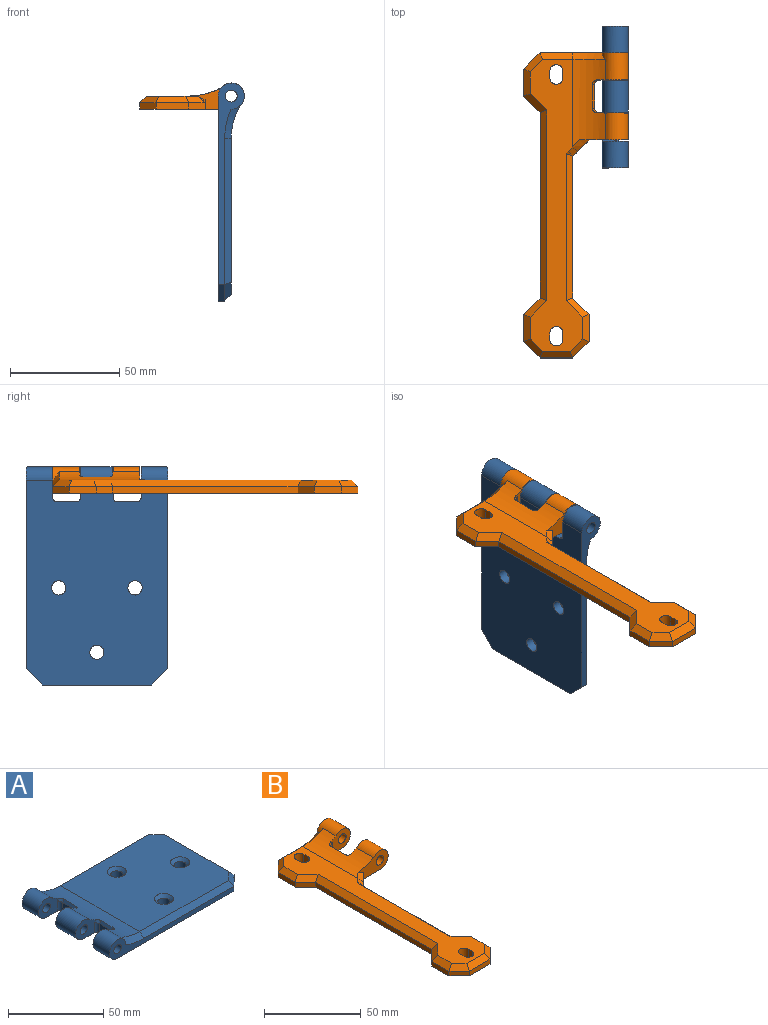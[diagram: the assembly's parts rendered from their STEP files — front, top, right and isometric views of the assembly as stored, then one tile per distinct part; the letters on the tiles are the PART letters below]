
ASSEMBLY  parts=2 mates=1
PART A: 43 faces, bbox 100x65x12 mm
  f0: plane 14.86x12mm, normal (0,-1,0), area 116.3mm2, adj f5,f9,f13,f16,f25,f30
  f1: plane 14.86x12mm, normal (0,1,0), area 116.3mm2, adj f9,f10,f15,f17,f27,f30
  f2: plane 14.86x12mm, normal (0,-1,0), area 116.3mm2, adj f4,f9,f14,f19,f28,f30
  f3: plane 14.86x12mm, normal (0,1,0), area 116.3mm2, adj f5,f9,f13,f18,f24,f30
  f4: cylinder r=6mm len=12.25mm, axis (0,-1,0), area 301.2mm2, adj f2,f6,f9,f30,f36
  f5: cylinder r=6mm len=14.8mm, axis (0,-1,0), area 355.9mm2, adj f0,f3,f9,f30
  f6: plane 92.5x12mm, normal (0,1,0), area 351mm2, adj f4,f9,f14,f35,f36,f37
  f7: plane 92.5x12mm, normal (0,-1,0), area 351mm2, adj f9,f10,f15,f34,f41,f42
  f8: plane 50x3mm, normal (1,0,0), area 150mm2, adj f9,f34,f35,f39
  f9: plane 94x65mm, normal (0,0,-1), area 5700.6mm2, adj f0,f1,f2,f3,f4,f5,f6,f7
  f10: cylinder r=6mm len=12.25mm, axis (0,-1,0), area 301.2mm2, adj f1,f7,f9,f30,f42
  f11: plane 8.85x5.44mm, normal (-1,0,0), area 48.2mm2, adj f9,f16,f17,f26
  f12: plane 8.85x5.44mm, normal (-1,0,0), area 48.2mm2, adj f9,f18,f19,f23
  f13: cylinder r=2.75mm len=14.8mm, axis (0,1,0), area 255.7mm2, adj f0,f3
  f14: cylinder r=2.75mm len=12.25mm, axis (0,1,0), area 211.7mm2, adj f2,f6
  f15: cylinder r=2.75mm len=12.25mm, axis (0,1,0), area 211.7mm2, adj f1,f7
  f16: cylinder r=2mm len=6.72mm, axis (0,0,-1), area 19.1mm2, adj f0,f9,f11,f25
  f17: cylinder r=2mm len=6.72mm, axis (0,0,1), area 19.1mm2, adj f1,f9,f11,f27
  f18: cylinder r=2mm len=6.72mm, axis (0,0,1), area 19.1mm2, adj f3,f9,f12,f24
  f19: cylinder r=2mm len=6.72mm, axis (0,0,-1), area 19.1mm2, adj f2,f9,f12,f28
  f20: cylinder r=3.25mm len=6.5mm, axis (0,0,1), area 86.8mm2, adj f9,f32
  f21: cylinder r=3.25mm len=6.5mm, axis (0,0,1), area 86.8mm2, adj f9,f31
  f22: cylinder r=3.25mm len=6.5mm, axis (0,0,1), area 86.8mm2, adj f9,f33
  f23: plane 8.85x1.76mm, normal (-0.87,0,0.48), area 17.8mm2, adj f12,f24,f28,f30
  f24: bspline ~3.7x3.45mm, area 5.9mm2, adj f3,f18,f23,f30
  f25: bspline ~3.7x3.45mm, area 5.9mm2, adj f0,f16,f26,f30
  f26: plane 8.85x1.76mm, normal (-0.87,0,0.48), area 17.8mm2, adj f11,f25,f27,f30
  f27: bspline ~3.7x3.45mm, area 5.9mm2, adj f1,f17,f26,f30
  f28: bspline ~3.7x3.45mm, area 5.9mm2, adj f2,f19,f23,f30
  f29: plane 71.53x59mm, normal (0,0,1), area 3951.8mm2, adj f30,f31,f32,f33,f37,f38,f39,f40
  f30: cylinder r=30.49mm len=59mm, axis (0,-1,0), area 748.4mm2, adj f0,f1,f2,f3,f4,f5,f10,f23
  f31: cone r=3.25mm half-angle=45deg, axis (0,0,1), area 64.1mm2, adj f21,f29
  f32: cone r=3.25mm half-angle=45deg, axis (0,0,1), area 64.1mm2, adj f20,f29
  f33: cone r=3.25mm half-angle=45deg, axis (0,0,1), area 64.1mm2, adj f22,f29
  f34: plane 7.5x7.5mm, normal (0.71,-0.71,0), area 31.8mm2, adj f7,f8,f9,f40
  f35: plane 7.5x7.5mm, normal (0.71,0.71,0), area 31.8mm2, adj f6,f8,f9,f38
  f36: cone r=33.49mm half-angle=45deg, axis (0,1,0), area 62.6mm2, adj f4,f6,f30,f37
  f37: plane 67.03x3mm, normal (0,0.71,0.71), area 281.8mm2, adj f6,f29,f36,f38
  f38: plane 8.74x8.74mm, normal (0.5,0.5,0.71), area 39.7mm2, adj f29,f35,f37,f39
  f39: plane 50x3mm, normal (0.71,0,0.71), area 206.9mm2, adj f8,f29,f38,f40
  f40: plane 8.74x8.74mm, normal (0.5,-0.5,0.71), area 39.7mm2, adj f29,f34,f39,f41
  f41: plane 67.03x3mm, normal (0,-0.71,0.71), area 281.8mm2, adj f7,f29,f40,f42
  f42: cone r=30.49mm half-angle=45deg, axis (0,-1,0), area 62.6mm2, adj f7,f10,f30,f41
PART B: 56 faces, bbox 48.1x140.1x39.2 mm
  f0: plane 22.51x12.05mm, normal (0,-1,0), area 151.7mm2, adj f3,f4,f5,f24,f38,f55
  f1: plane 14.26x12mm, normal (0,-1,0), area 111.7mm2, adj f3,f28,f29,f31,f36,f38
  f2: plane 14.26x12mm, normal (0,1,0), area 111.7mm2, adj f3,f4,f5,f32,f34,f38
  f3: plane 140x42mm, normal (0,0,-1), area 3125.3mm2, adj f0,f1,f2,f4,f6,f7,f8,f9
  f4: cylinder r=6mm len=12.5mm, axis (0,1,0), area 300.6mm2, adj f0,f2,f3,f38
  f5: cylinder r=2.75mm len=12.5mm, axis (0,1,0), area 216mm2, adj f0,f2
  f6: cylinder r=3mm len=6mm, axis (0,0,-1), area 56.5mm2, adj f3,f7,f20,f37
  f7: plane 6x3mm, normal (-1,0,0), area 18mm2, adj f3,f6,f8,f37
  f8: cylinder r=3mm len=6mm, axis (0,0,-1), area 56.5mm2, adj f3,f7,f20,f37
  f9: cylinder r=3mm len=6mm, axis (0,0,-1), area 56.5mm2, adj f3,f10,f19,f37
  f10: plane 6x3mm, normal (1,0,0), area 18mm2, adj f3,f9,f11,f37
  f11: cylinder r=3mm len=6mm, axis (0,0,-1), area 56.5mm2, adj f3,f10,f19,f37
  f12: plane 65x3mm, normal (1,0,0), area 195mm2, adj f3,f21,f24,f52
  f13: plane 40.5x12mm, normal (0,1,0), area 195mm2, adj f3,f27,f28,f29,f39,f40
  f14: plane 12.5x3mm, normal (-1,0,0), area 37.5mm2, adj f3,f23,f27,f42
  f15: plane 85x3mm, normal (-1,0,0), area 255mm2, adj f3,f22,f23,f44
  f16: plane 12.5x3mm, normal (-1,0,0), area 37.5mm2, adj f3,f22,f26,f46
  f17: plane 15x3mm, normal (0,-1,0), area 45mm2, adj f3,f25,f26,f48
  f18: plane 12.5x3mm, normal (1,0,0), area 37.5mm2, adj f3,f21,f25,f50
  f19: plane 6x3mm, normal (-1,0,0), area 18mm2, adj f3,f9,f11,f37
  f20: plane 6x3mm, normal (1,0,0), area 18mm2, adj f3,f6,f8,f37
  f21: plane 7.5x7.5mm, normal (0.71,0.71,0), area 31.8mm2, adj f3,f12,f18,f51
  f22: plane 7.5x7.5mm, normal (-0.71,0.71,0), area 31.8mm2, adj f3,f15,f16,f45
  f23: plane 7.5x7.5mm, normal (-0.71,-0.71,0), area 31.8mm2, adj f3,f14,f15,f43
  f24: plane 7.55x7.55mm, normal (0.71,-0.71,0), area 36.7mm2, adj f0,f3,f12,f33,f53,f55
  f25: plane 7.5x7.5mm, normal (0.71,-0.71,0), area 31.8mm2, adj f3,f17,f18,f49
  f26: plane 7.5x7.5mm, normal (-0.71,-0.71,0), area 31.8mm2, adj f3,f16,f17,f47
  f27: plane 7.5x7.5mm, normal (-0.71,0.71,0), area 31.8mm2, adj f3,f13,f14,f41
  f28: cylinder r=6mm len=12.5mm, axis (0,1,0), area 307.2mm2, adj f1,f3,f13,f38,f39
  f29: cylinder r=2.75mm len=12.5mm, axis (0,1,0), area 216mm2, adj f1,f13
  f30: plane 11x5.75mm, normal (1,0,0), area 63.3mm2, adj f3,f31,f32,f35
  f31: cylinder r=2mm len=7.12mm, axis (0,0,-1), area 20.2mm2, adj f1,f3,f30,f36
  f32: cylinder r=2mm len=7.12mm, axis (0,0,1), area 20.2mm2, adj f2,f3,f30,f34
  f33: bspline ~39.11x39.11mm, area 0.4mm2, adj f24,f54,f55
  f34: bspline ~3.73x3.53mm, area 5.4mm2, adj f2,f32,f35,f38
  f35: plane 11x1.62mm, normal (0.86,0,0.51), area 20.7mm2, adj f30,f34,f36,f38
  f36: bspline ~3.73x3.53mm, area 5.4mm2, adj f1,f31,f35,f38
  f37: plane 134x24mm, normal (0,0,1), area 1629.5mm2, adj f6,f7,f8,f9,f10,f11,f19,f20
  f38: cylinder r=30.49mm len=40.23mm, axis (0,1,0), area 489.5mm2, adj f0,f1,f2,f4,f28,f34,f35,f36
  f39: cone r=30.49mm half-angle=45deg, axis (0,1,0), area 62.6mm2, adj f13,f28,f38,f40
  f40: plane 15.03x3mm, normal (0,0.71,0.71), area 61.1mm2, adj f13,f37,f39,f41
  f41: plane 8.74x8.74mm, normal (-0.5,0.5,0.71), area 39.7mm2, adj f27,f37,f40,f42
  f42: plane 12.5x3mm, normal (-0.71,0,0.71), area 47.8mm2, adj f14,f37,f41,f43
  f43: plane 10.5x8.74mm, normal (-0.5,-0.5,0.71), area 45mm2, adj f23,f37,f42,f44
  f44: plane 87.49x3mm, normal (-0.71,0,0.71), area 365.9mm2, adj f15,f37,f43,f45
  f45: plane 10.5x8.74mm, normal (-0.5,0.5,0.71), area 45mm2, adj f22,f37,f44,f46
  f46: plane 12.5x3mm, normal (-0.71,0,0.71), area 47.8mm2, adj f16,f37,f45,f47
  f47: plane 8.74x8.74mm, normal (-0.5,-0.5,0.71), area 39.7mm2, adj f26,f37,f46,f48
  f48: plane 15x3mm, normal (0,-0.71,0.71), area 58.4mm2, adj f17,f37,f47,f49
  f49: plane 8.74x8.74mm, normal (0.5,-0.5,0.71), area 39.7mm2, adj f25,f37,f48,f50
  f50: plane 12.5x3mm, normal (0.71,0,0.71), area 47.8mm2, adj f18,f37,f49,f51
  f51: plane 10.5x8.74mm, normal (0.5,0.5,0.71), area 45mm2, adj f21,f37,f50,f52
  f52: plane 67.49x3mm, normal (0.71,0,0.71), area 281mm2, adj f12,f37,f51,f53
  f53: plane 3.03x3mm, normal (0.5,-0.5,0.71), area 2.8mm2, adj f24,f37,f52,f54
  f54: bspline ~4.24x4.23mm, area 12.5mm2, adj f33,f37,f53,f55
  f55: bspline ~7.52x7.51mm, area 24.1mm2, adj f0,f24,f33,f38,f54
PLACE A rot(axis=(0,1,0),90deg) t=(-24.44,-24.9,77.28)mm
PLACE B t=(-45.44,-94.06,-1.52)mm
MATE revolute A.f4 <-> B.f4  axis (0,-1,0) through (-18.44,61.65,4.48)mm
